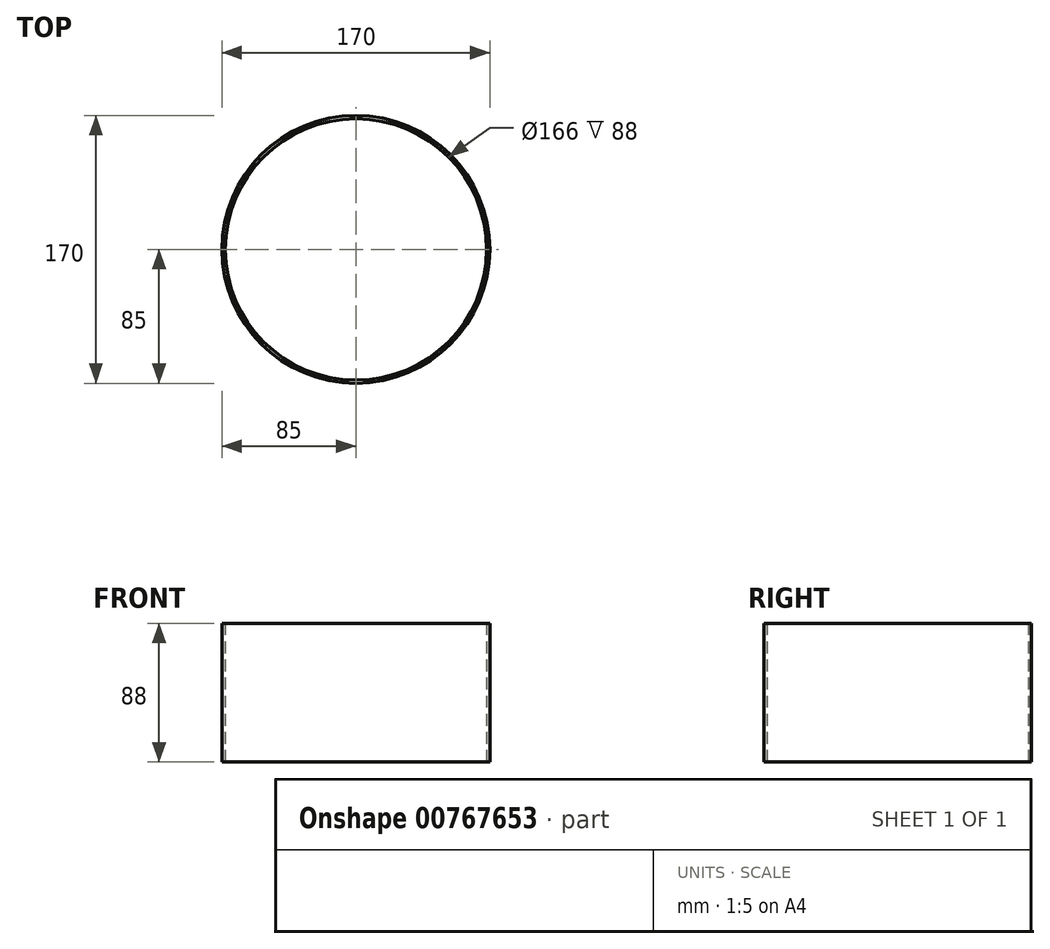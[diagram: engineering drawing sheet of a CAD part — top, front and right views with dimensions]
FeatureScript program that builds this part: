
annotation { "Feature Type Name" : "Feature", "Feature Type Description" : "" }
export const myFeature = defineFeature(function(context is Context, id is Id, definition is map)
    precondition{}
    {
        {
            var Q0;
            Q0=qCreatedBy(makeId("Front.planeOp"),FACE);
            var sketch = newSketch(context, id + "F0", { "sketchPlane" : qUnion([Q0])});
            skLineSegment(sketch, "E0", {"start": v(-83, 0) * mm, "end": v(-85, 0) * mm});
            skLineSegment(sketch, "E1", {"start": v(-85, 0) * mm, "end": v(-85, 88) * mm});
            skLineSegment(sketch, "E2", {"start": v(-85, 88) * mm, "end": v(-85, 88) * mm});
            skLineSegment(sketch, "E3", {"start": v(-83, 88) * mm, "end": v(-83, 0) * mm});
            skLineSegment(sketch, "E4", {"start": v(0, 0) * mm, "end": v(0, 29.31) * mm, "construction": true});
            skLineSegment(sketch, "E5", {"start": v(-85, 88) * mm, "end": v(-83, 88) * mm});
            skSolve(sketch);
        }
        {
            var Q0;
            Q0=makeQuery(id+"F0.imprint","IMPRINT",FACE,{"disambiguationData":[TD([[makeQuery(id+"F0.imprint","IMPRINT",EDGE,{"derivedFrom":sQuery(id+"F0.wireOp",EDGE,"E0")}),-1.0]])]});
            var Q1;
            Q1=sQuery(id+"F0.wireOp",EDGE,"E4");
            revolve(context, id + "F1", {"surfaceOperationType" : NewSurfaceOperationType.NEW, "entities" : qUnion([Q0]), "axis" : qUnion([Q1]), "revolveType" : RevolveType.FULL});
        }
    });
